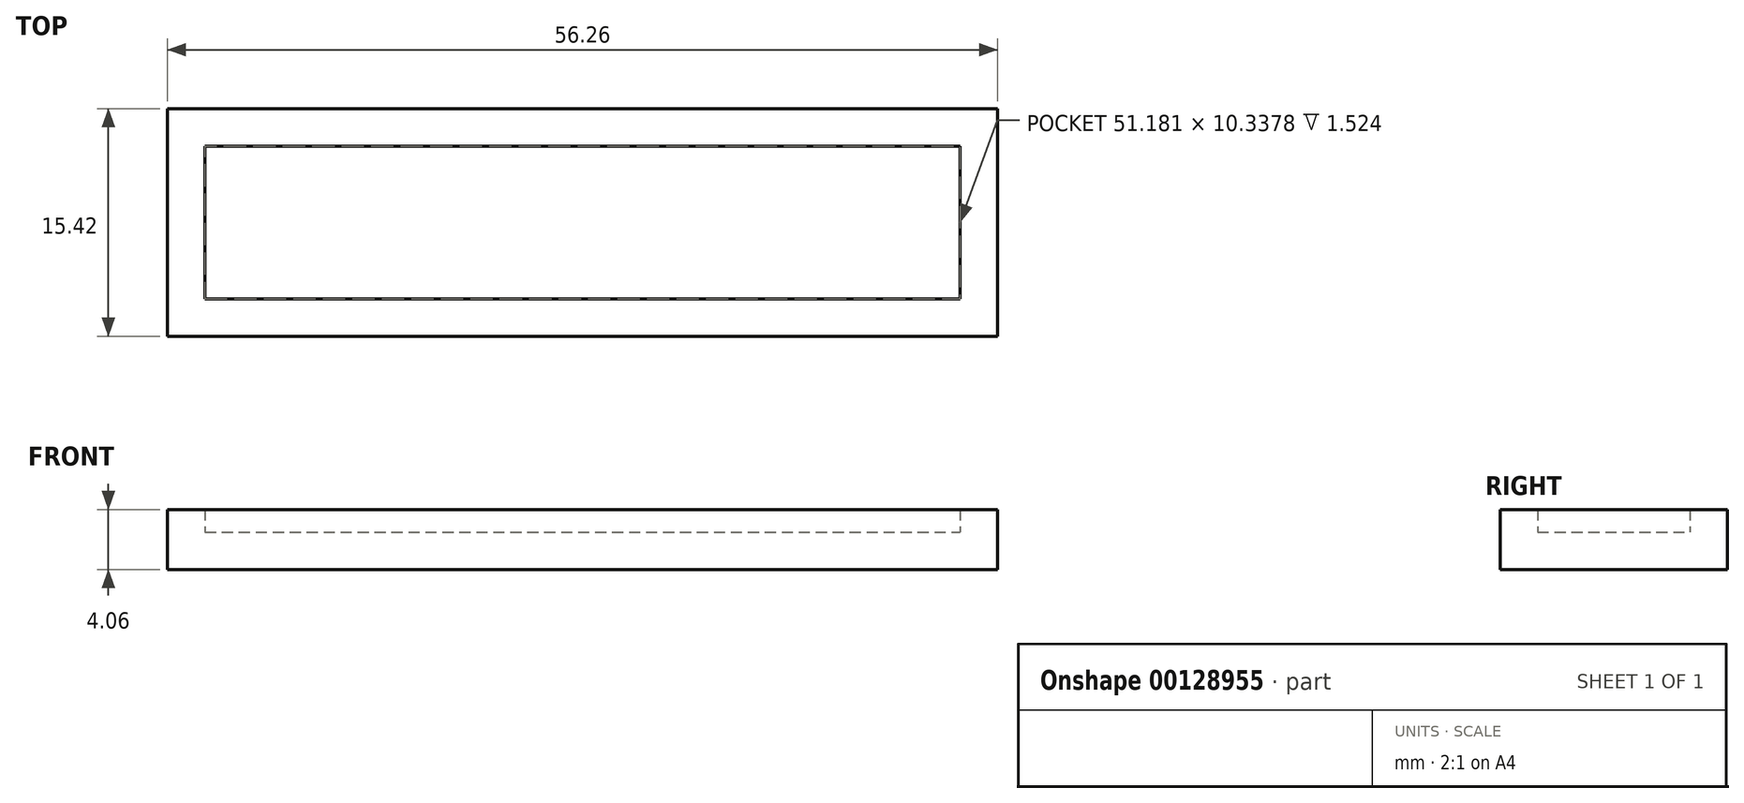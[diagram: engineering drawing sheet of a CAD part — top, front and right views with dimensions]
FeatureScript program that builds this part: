
annotation { "Feature Type Name" : "Feature", "Feature Type Description" : "" }
export const myFeature = defineFeature(function(context is Context, id is Id, definition is map)
    precondition{}
    {
        {
            var Q0;
            Q0=qCreatedBy(makeId("Top.planeOp"),FACE);
            var sketch = newSketch(context, id + "F0", { "sketchPlane" : qUnion([Q0])});
            skLineSegment(sketch, "E0.bottom", {"start": v(25.6, 5.17) * mm, "end": v(-25.6, 5.17) * mm});
            skLineSegment(sketch, "E0.top", {"start": v(25.6, -5.17) * mm, "end": v(-25.6, -5.17) * mm});
            skLineSegment(sketch, "E0.left", {"start": v(25.6, 5.17) * mm, "end": v(25.6, -5.17) * mm});
            skLineSegment(sketch, "E0.right", {"start": v(-25.6, 5.17) * mm, "end": v(-25.6, -5.17) * mm});
            skPoint(sketch, "E0.middle", {"position": v(0, 0) * mm});
            skLineSegment(sketch, "E1.0", {"start": v(28.13, 7.7) * mm, "end": v(-28.13, 7.7) * mm});
            skLineSegment(sketch, "E1.1", {"start": v(28.13, 7.7) * mm, "end": v(28.13, -7.7) * mm});
            skLineSegment(sketch, "E1.2", {"start": v(28.13, -7.7) * mm, "end": v(-28.13, -7.7) * mm});
            skLineSegment(sketch, "E1.3", {"start": v(-28.13, 7.7) * mm, "end": v(-28.13, -7.7) * mm});
            skSolve(sketch);
        }
        {
            var Q0;
            Q0 = qSketchRegion(id + "F0", true);
            var Q1;
            Q1=makeQuery(id+"F0.imprint","IMPRINT",FACE,{"disambiguationData":[TD([[makeQuery(id+"F0.imprint","IMPRINT",EDGE,{"derivedFrom":sQuery(id+"F0.wireOp",EDGE,"E0.bottom")}),1.0]])]});
            var Q2;
            Q2=makeQuery(id+"F0.imprint","IMPRINT",FACE,{"disambiguationData":[TD([[makeQuery(id+"F0.imprint","IMPRINT",EDGE,{"derivedFrom":sQuery(id+"F0.wireOp",EDGE,"27N3irfc-3kMl-QchH-mz6c-2AM9bB8Ep1Gc")}),1.0]])]});
            var Q3;
            Q3=makeQuery(id+"F0.imprint","IMPRINT",FACE,{"disambiguationData":[TD([[makeQuery(id+"F0.imprint","IMPRINT",EDGE,{"derivedFrom":sQuery(id+"F0.wireOp",EDGE,"98IZvntY-elp5-F0Pq-gjuy-yX4lAncdEuou")}),1.0]])]});
            extrude(context, id + "F1", {"entities" : qUnion([Q0, Q1, Q2, Q3]), "depth" : 2.54 * mm, "symmetric" : true});
        }
        {
            var Q0;
            Q0=makeQuery(id+"F0.imprint","IMPRINT",FACE,{"disambiguationData":[TD([[makeQuery(id+"F0.imprint","IMPRINT",EDGE,{"derivedFrom":sQuery(id+"F0.wireOp",EDGE,"27N3irfc-3kMl-QchH-mz6c-2AM9bB8Ep1Gc")}),1.0]])]});
            var Q1;
            Q1=makeQuery(id+"F0.imprint","IMPRINT",FACE,{"disambiguationData":[TD([[makeQuery(id+"F0.imprint","IMPRINT",EDGE,{"derivedFrom":sQuery(id+"F0.wireOp",EDGE,"98IZvntY-elp5-F0Pq-gjuy-yX4lAncdEuou")}),1.0]])]});
            var Q2;
            Q2=makeQuery(id+"F0.imprint","IMPRINT",FACE,{"disambiguationData":[TD([[makeQuery(id+"F0.imprint","IMPRINT",EDGE,{"derivedFrom":sQuery(id+"F0.wireOp",EDGE,"E0.bottom")}),-1.0]])]});
            extrude(context, id + "F2", {"entities" : qUnion([Q0, Q1, Q2]), "operationType" : NewBodyOperationType.ADD, "depth" : 2.8 * mm});
        }
    });
